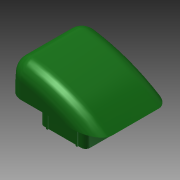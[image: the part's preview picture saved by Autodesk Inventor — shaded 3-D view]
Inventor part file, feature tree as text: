
AUTODESK INVENTOR PART (.ipt)
format: ipt  version: 2015 (Build 190159000, 159)  size: 266,752 bytes
history: native  units: in
note: dims shown in document units (in); Inventor stores cm internally (conversion verified against a paired STEP export)
features: sketch x3, extrude x2, fillet x2, shell x2, plane x1
ambient origin geometry x8: Origin, YZ Plane, XZ Plane, XY Plane, X Axis, Y Axis, Z Axis, Center Point
bodies: Solid1 (feature_tree)
feature tree (10):
  extrude  "Extrusion1"  Depth=0.5in
  fillet  "Fillet1"  Radius=0.5in
  fillet  "Fillet2"  Radius=0.07in
  shell  "Shell1"  Thickness=0.67in
  plane  "Work Plane1"
  sketch  "Sketch2"  dims[d58=1.0in d59=0.0in d60=0.05in]
  extrude  "Extrusion3"  Depth=0.05in
  shell  "Shell3"  [1 undecoded]
  sketch  "Sketch1"  dims[d10=2.55in d11=0.0in d12=0.5in d13=0.5in d14=0.07in d15=0.67in]
  sketch  "Sketch3"
note: 1 required parameter value undecoded (feature->parameter linkage not recoverable at this tier; creation-order binding heuristic only, values carry confidence <= 0.55)
